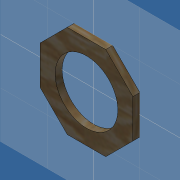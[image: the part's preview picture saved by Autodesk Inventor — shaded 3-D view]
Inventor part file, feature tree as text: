
AUTODESK INVENTOR PART (.ipt)
format: ipt  version: 2019 (Build 230136000, 136)  size: 115,200 bytes
history: native  units: mm
features: other x1, extrude x1, sketch x1
ambient origin geometry x8: Origin, YZ Plane, XZ Plane, XY Plane, X Axis, Y Axis, Z Axis, Center Point
bodies: Body1 (feature_tree)
feature tree (3):
  other  "<userpath>\OneDrive\Dokumente\Inventor\Absauganlage\Absauganlage_Params.xlsx"
  extrude  "Extrusion2"  Depth=15.0mm TaperAngle=0.0deg
  sketch  "Skizze2"  dims[d6=135.0mm d8=15.0mm d9=0.0mm d10=200.0mm]
